# Revit family: Zahnbolzen
name_source: partatom
category: HLS-Bauteile
revit_build: Autodesk Revit 2017 (Build: 20190507_1515(x64)
units: mm (PartAtom-declared; Revit-internal decimal feet)

## family parameters
Arbeitsebenenbasiert = Ja
Beim Laden mit Abzugskörper schneiden = Nein
Bemaßung runder Anschluss = Durchmesser verwenden
Gemeinsam genutzt = Ja
Immer vertikal = Nein
Raumberechnungspunkt = Nein
Teiletyp = Normal

## types (3) — shared parameters
Anzugsmoment = 0.00 kN-m
Fabrikat = MEFA
Firma = MEFA Befestigungs- und Montagesysteme GmbH
Kurztext1 = Zahnbolzen C-Profil 45
Material = Stahl
Materialname = S235
Mengeneinheit = St
Oberflaeche = galvanisch verzinkt
Profiltyp = 45
Vorgabe-Ansicht = 1219 mm
vpe = 100 St
zero-valued in all types: Breite, Länge, Stärke Material

## per-type parameters (varying)
| type | Abmessung | Artikelnummer | EAN | Gewicht | Gewicht pro Bauteil | Gewinde | Gewindestift | Kurztext2 | Zahnplatte |
| Zahnbolzen M 8 | M8 x 17,5 mm | 0816936 | 4250928420510 | 0.07 kg | 0.07 kg | M8 | Gewindestifte : Gewindestift M8x35 | M8 x 17,5 mm | MEFA Zahnplatte S : MEFA Zahnplatte S M 8 |
| Zahnbolzen M10 | M10 x 19,5 mm | 0816944 | 4250928449177 | 0.08 kg | 0.08 kg | M10 | Gewindestifte : Gewindestift M10x35 | M10 x 19,5 mm | MEFA Zahnplatte S : MEFA Zahnplatte S M10 |
| Zahnbolzen M12 | M12 x 22,5 mm | 0816952 | 4250928420534 | 0.08 kg | 0.08 kg | M12 | Gewindestifte : Gewindestift M12x40 | M12 x 22,5 mm | MEFA Zahnplatte S : MEFA Zahnplatte S M12 |
